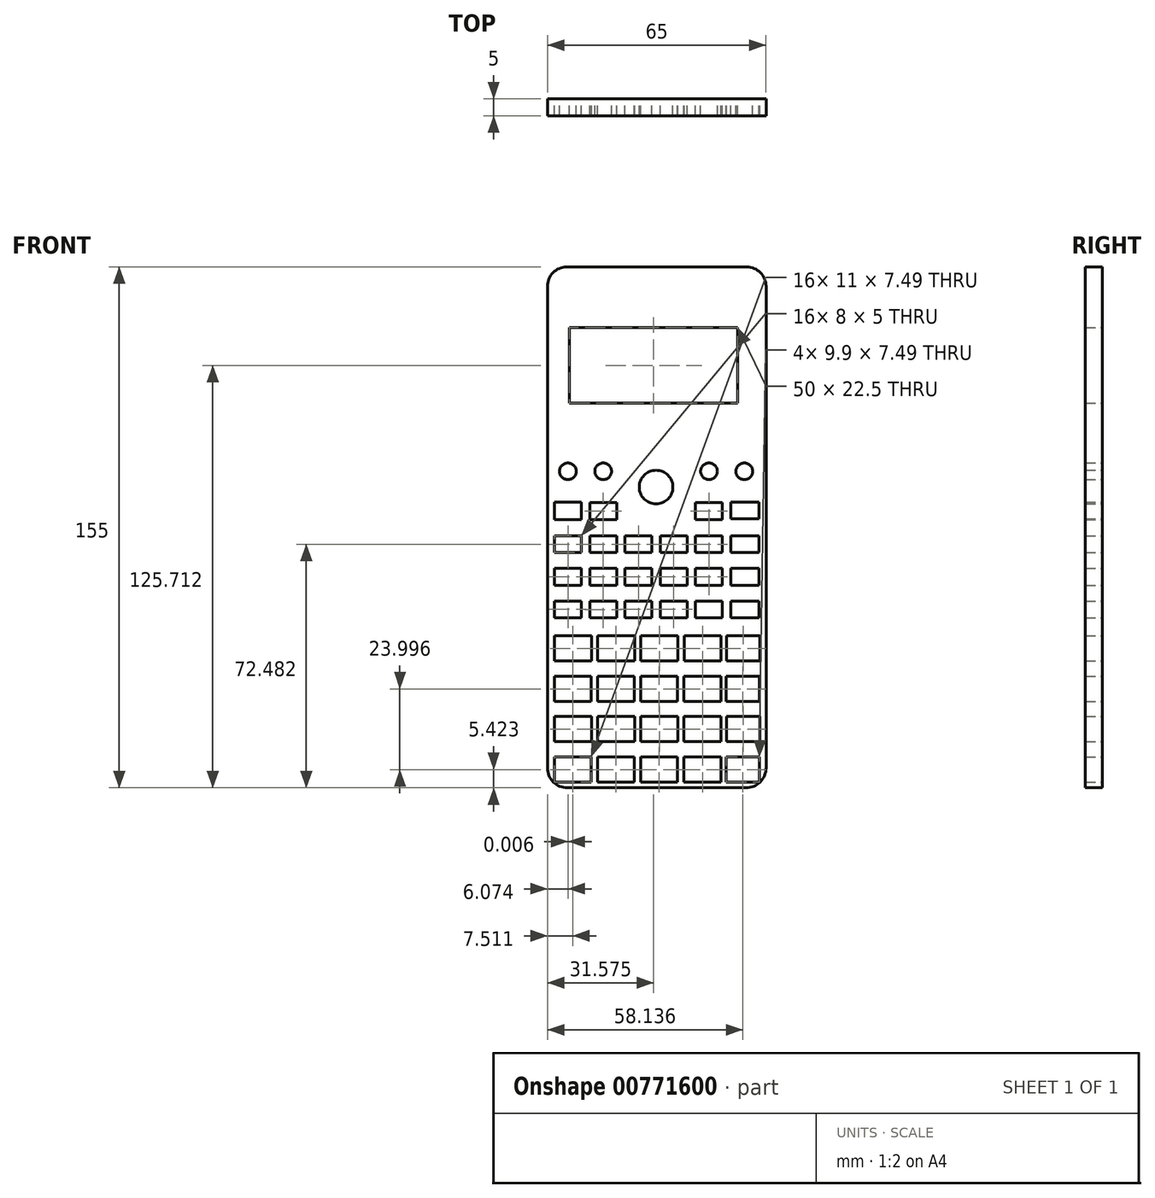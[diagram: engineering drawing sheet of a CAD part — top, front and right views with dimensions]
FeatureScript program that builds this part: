
annotation { "Feature Type Name" : "Feature", "Feature Type Description" : "" }
export const myFeature = defineFeature(function(context is Context, id is Id, definition is map)
    precondition{}
    {
        {
            var Q0;
            Q0=qCreatedBy(makeId("Front.planeOp"),FACE);
            var sketch = newSketch(context, id + "F0", { "sketchPlane" : qUnion([Q0])});
            skLineSegment(sketch, "E0.bottom", {"start": v(-32.07, 54.27) * mm, "end": v(32.93, 54.27) * mm});
            skLineSegment(sketch, "E0.top", {"start": v(-26.1, -45.56) * mm, "end": v(26.97, -45.56) * mm});
            skLineSegment(sketch, "E0.left", {"start": v(-32.07, 54.27) * mm, "end": v(-32.07, -39.6) * mm});
            skLineSegment(sketch, "E0.right", {"start": v(32.93, 54.27) * mm, "end": v(32.93, -39.6) * mm});
            skPoint(sketch, "E1.visualSharp", {"position": v(32.93, -45.56) * mm});
            skArc(sketch, "E1.filletArc", {"start": v(26.97, -45.56) * mm, "mid": v(31.19, -43.81) * mm, "end": v(32.93, -39.6) * mm});
            skPoint(sketch, "E2.visualSharp", {"position": v(-32.07, -45.56) * mm});
            skArc(sketch, "E2.filletArc", {"start": v(-32.07, -39.6) * mm, "mid": v(-30.32, -43.81) * mm, "end": v(-26.1, -45.56) * mm});
            skLineSegment(sketch, "E3", {"start": v(-30.06, -43.88) * mm, "end": v(-19.06, -43.88) * mm});
            skLineSegment(sketch, "E4", {"start": v(-19.06, -43.88) * mm, "end": v(-19.06, -36.4) * mm});
            skLineSegment(sketch, "E5", {"start": v(-19.06, -36.4) * mm, "end": v(-30.06, -36.4) * mm});
            skLineSegment(sketch, "E6", {"start": v(-30.06, -36.4) * mm, "end": v(-30.06, -43.88) * mm});
            skLineSegment(sketch, "E7", {"start": v(-30.06, -43.88) * mm, "end": v(-24.56, -43.88) * mm});
            skLineSegment(sketch, "E8", {"start": v(-17.22, -43.88) * mm, "end": v(-6.22, -43.88) * mm});
            skLineSegment(sketch, "E9", {"start": v(-6.22, -43.88) * mm, "end": v(-6.22, -36.4) * mm});
            skLineSegment(sketch, "E10", {"start": v(-6.22, -36.4) * mm, "end": v(-17.22, -36.4) * mm});
            skLineSegment(sketch, "E11", {"start": v(-17.22, -36.4) * mm, "end": v(-17.22, -43.88) * mm});
            skLineSegment(sketch, "E12", {"start": v(-17.22, -43.88) * mm, "end": v(-11.72, -43.88) * mm});
            skLineSegment(sketch, "E13", {"start": v(-4.36, -43.88) * mm, "end": v(6.63, -43.88) * mm});
            skLineSegment(sketch, "E14", {"start": v(6.63, -43.88) * mm, "end": v(6.63, -36.4) * mm});
            skLineSegment(sketch, "E15", {"start": v(6.63, -36.4) * mm, "end": v(-4.36, -36.4) * mm});
            skLineSegment(sketch, "E16", {"start": v(-4.36, -36.4) * mm, "end": v(-4.36, -43.88) * mm});
            skLineSegment(sketch, "E17", {"start": v(-4.36, -43.88) * mm, "end": v(1.14, -43.88) * mm});
            skLineSegment(sketch, "E18", {"start": v(8.52, -43.88) * mm, "end": v(19.52, -43.88) * mm});
            skLineSegment(sketch, "E19", {"start": v(19.52, -43.88) * mm, "end": v(19.52, -36.4) * mm});
            skLineSegment(sketch, "E20", {"start": v(19.52, -36.4) * mm, "end": v(8.52, -36.4) * mm});
            skLineSegment(sketch, "E21", {"start": v(8.52, -36.4) * mm, "end": v(8.52, -43.88) * mm});
            skLineSegment(sketch, "E22", {"start": v(8.52, -43.88) * mm, "end": v(14.02, -43.88) * mm});
            skLineSegment(sketch, "E23", {"start": v(21.12, -43.88) * mm, "end": v(31.02, -43.88) * mm});
            skLineSegment(sketch, "E24", {"start": v(31.02, -43.88) * mm, "end": v(31.02, -36.4) * mm});
            skLineSegment(sketch, "E25", {"start": v(31.02, -36.4) * mm, "end": v(21.12, -36.4) * mm});
            skLineSegment(sketch, "E26", {"start": v(21.12, -36.4) * mm, "end": v(21.12, -43.88) * mm});
            skLineSegment(sketch, "E27", {"start": v(21.12, -43.88) * mm, "end": v(25.78, -43.88) * mm});
            skLineSegment(sketch, "E28", {"start": v(-30, -31.8) * mm, "end": v(-19, -31.8) * mm});
            skLineSegment(sketch, "E29", {"start": v(-19, -31.8) * mm, "end": v(-19, -24.3) * mm});
            skLineSegment(sketch, "E30", {"start": v(-19, -24.3) * mm, "end": v(-30, -24.3) * mm});
            skLineSegment(sketch, "E31", {"start": v(-30, -24.3) * mm, "end": v(-30, -31.8) * mm});
            skLineSegment(sketch, "E32", {"start": v(-30, -31.8) * mm, "end": v(-24.5, -31.8) * mm});
            skLineSegment(sketch, "E33", {"start": v(-17.15, -31.8) * mm, "end": v(-6.16, -31.8) * mm});
            skLineSegment(sketch, "E34", {"start": v(-6.16, -31.8) * mm, "end": v(-6.16, -24.3) * mm});
            skLineSegment(sketch, "E35", {"start": v(-6.16, -24.3) * mm, "end": v(-17.15, -24.3) * mm});
            skLineSegment(sketch, "E36", {"start": v(-17.15, -24.3) * mm, "end": v(-17.15, -31.8) * mm});
            skLineSegment(sketch, "E37", {"start": v(-17.15, -31.8) * mm, "end": v(-11.66, -31.8) * mm});
            skLineSegment(sketch, "E38", {"start": v(-4.3, -31.8) * mm, "end": v(6.7, -31.8) * mm});
            skLineSegment(sketch, "E39", {"start": v(6.7, -31.8) * mm, "end": v(6.7, -24.3) * mm});
            skLineSegment(sketch, "E40", {"start": v(6.7, -24.3) * mm, "end": v(-4.3, -24.3) * mm});
            skLineSegment(sketch, "E41", {"start": v(-4.3, -24.3) * mm, "end": v(-4.3, -31.8) * mm});
            skLineSegment(sketch, "E42", {"start": v(-4.3, -31.8) * mm, "end": v(1.2, -31.8) * mm});
            skLineSegment(sketch, "E43", {"start": v(21.18, -31.8) * mm, "end": v(31.08, -31.8) * mm});
            skLineSegment(sketch, "E44", {"start": v(31.08, -31.8) * mm, "end": v(31.08, -24.3) * mm});
            skLineSegment(sketch, "E45", {"start": v(31.08, -24.3) * mm, "end": v(21.18, -24.3) * mm});
            skLineSegment(sketch, "E46", {"start": v(21.18, -24.3) * mm, "end": v(21.18, -31.8) * mm});
            skLineSegment(sketch, "E47", {"start": v(21.18, -31.8) * mm, "end": v(25.84, -31.8) * mm});
            skPoint(sketch, "E48.visualSharp", {"position": v(-32.07, -21.72) * mm});
            skLineSegment(sketch, "E49", {"start": v(-30.06, -19.89) * mm, "end": v(-19.06, -19.89) * mm});
            skLineSegment(sketch, "E50", {"start": v(-19.06, -19.89) * mm, "end": v(-19.06, -12.4) * mm});
            skLineSegment(sketch, "E51", {"start": v(-19.06, -12.4) * mm, "end": v(-30.06, -12.4) * mm});
            skLineSegment(sketch, "E52", {"start": v(-30.06, -12.4) * mm, "end": v(-30.06, -19.89) * mm});
            skLineSegment(sketch, "E53", {"start": v(-30.06, -19.89) * mm, "end": v(-24.56, -19.89) * mm});
            skLineSegment(sketch, "E54", {"start": v(-17.22, -19.89) * mm, "end": v(-6.22, -19.89) * mm});
            skLineSegment(sketch, "E55", {"start": v(-6.22, -19.89) * mm, "end": v(-6.22, -12.4) * mm});
            skLineSegment(sketch, "E56", {"start": v(-6.22, -12.4) * mm, "end": v(-17.22, -12.4) * mm});
            skLineSegment(sketch, "E57", {"start": v(-17.22, -12.4) * mm, "end": v(-17.22, -19.89) * mm});
            skLineSegment(sketch, "E58", {"start": v(-17.22, -19.89) * mm, "end": v(-11.72, -19.89) * mm});
            skLineSegment(sketch, "E59", {"start": v(-4.36, -19.89) * mm, "end": v(6.63, -19.89) * mm});
            skLineSegment(sketch, "E60", {"start": v(6.63, -19.89) * mm, "end": v(6.63, -12.4) * mm});
            skLineSegment(sketch, "E61", {"start": v(6.63, -12.4) * mm, "end": v(-4.36, -12.4) * mm});
            skLineSegment(sketch, "E62", {"start": v(-4.36, -12.4) * mm, "end": v(-4.36, -19.89) * mm});
            skLineSegment(sketch, "E63", {"start": v(-4.36, -19.89) * mm, "end": v(1.14, -19.89) * mm});
            skLineSegment(sketch, "E64", {"start": v(8.52, -19.89) * mm, "end": v(19.52, -19.89) * mm});
            skLineSegment(sketch, "E65", {"start": v(19.52, -19.89) * mm, "end": v(19.52, -12.4) * mm});
            skLineSegment(sketch, "E66", {"start": v(19.52, -12.4) * mm, "end": v(8.52, -12.4) * mm});
            skLineSegment(sketch, "E67", {"start": v(8.52, -12.4) * mm, "end": v(8.52, -19.89) * mm});
            skLineSegment(sketch, "E68", {"start": v(8.52, -19.89) * mm, "end": v(14.02, -19.89) * mm});
            skLineSegment(sketch, "E69", {"start": v(21.12, -19.89) * mm, "end": v(31.02, -19.89) * mm});
            skLineSegment(sketch, "E70", {"start": v(31.02, -19.89) * mm, "end": v(31.02, -12.4) * mm});
            skLineSegment(sketch, "E71", {"start": v(31.02, -12.4) * mm, "end": v(21.12, -12.4) * mm});
            skLineSegment(sketch, "E72", {"start": v(21.12, -12.4) * mm, "end": v(21.12, -19.89) * mm});
            skLineSegment(sketch, "E73", {"start": v(21.12, -19.89) * mm, "end": v(25.78, -19.89) * mm});
            skLineSegment(sketch, "E74", {"start": v(-30, -7.8) * mm, "end": v(-19, -7.8) * mm});
            skLineSegment(sketch, "E75", {"start": v(-19, -7.8) * mm, "end": v(-19, -0.31) * mm});
            skLineSegment(sketch, "E76", {"start": v(-19, -0.31) * mm, "end": v(-30, -0.31) * mm});
            skLineSegment(sketch, "E77", {"start": v(-30, -0.31) * mm, "end": v(-30, -7.8) * mm});
            skLineSegment(sketch, "E78", {"start": v(-30, -7.8) * mm, "end": v(-24.5, -7.8) * mm});
            skLineSegment(sketch, "E79", {"start": v(-17.15, -7.8) * mm, "end": v(-6.16, -7.8) * mm});
            skLineSegment(sketch, "E80", {"start": v(-6.16, -7.8) * mm, "end": v(-6.16, -0.31) * mm});
            skLineSegment(sketch, "E81", {"start": v(-6.16, -0.31) * mm, "end": v(-17.15, -0.31) * mm});
            skLineSegment(sketch, "E82", {"start": v(-17.15, -0.31) * mm, "end": v(-17.15, -7.8) * mm});
            skLineSegment(sketch, "E83", {"start": v(-17.15, -7.8) * mm, "end": v(-11.66, -7.8) * mm});
            skLineSegment(sketch, "E84", {"start": v(-4.3, -7.8) * mm, "end": v(6.7, -7.8) * mm});
            skLineSegment(sketch, "E85", {"start": v(6.7, -7.8) * mm, "end": v(6.7, -0.31) * mm});
            skLineSegment(sketch, "E86", {"start": v(6.7, -0.31) * mm, "end": v(-4.3, -0.31) * mm});
            skLineSegment(sketch, "E87", {"start": v(-4.3, -0.31) * mm, "end": v(-4.3, -7.8) * mm});
            skLineSegment(sketch, "E88", {"start": v(-4.3, -7.8) * mm, "end": v(1.2, -7.8) * mm});
            skLineSegment(sketch, "E89", {"start": v(8.58, -7.8) * mm, "end": v(19.58, -7.8) * mm});
            skLineSegment(sketch, "E90", {"start": v(19.58, -7.8) * mm, "end": v(19.58, -0.31) * mm});
            skLineSegment(sketch, "E91", {"start": v(19.58, -0.31) * mm, "end": v(8.58, -0.31) * mm});
            skLineSegment(sketch, "E92", {"start": v(8.58, -0.31) * mm, "end": v(8.58, -7.8) * mm});
            skLineSegment(sketch, "E93", {"start": v(8.58, -7.8) * mm, "end": v(14.08, -7.8) * mm});
            skLineSegment(sketch, "E94", {"start": v(21.18, -7.8) * mm, "end": v(31.08, -7.8) * mm});
            skLineSegment(sketch, "E95", {"start": v(31.08, -7.8) * mm, "end": v(31.08, -0.31) * mm});
            skLineSegment(sketch, "E96", {"start": v(31.08, -0.31) * mm, "end": v(21.18, -0.31) * mm});
            skLineSegment(sketch, "E97", {"start": v(21.18, -0.31) * mm, "end": v(21.18, -7.8) * mm});
            skLineSegment(sketch, "E98", {"start": v(21.18, -7.8) * mm, "end": v(25.84, -7.8) * mm});
            skLineSegment(sketch, "E99", {"start": v(-30, 5.02) * mm, "end": v(-21.99, 5.02) * mm});
            skLineSegment(sketch, "E100", {"start": v(-21.99, 5.02) * mm, "end": v(-21.99, 10.02) * mm});
            skLineSegment(sketch, "E101", {"start": v(-21.99, 10.02) * mm, "end": v(-30, 10.02) * mm});
            skLineSegment(sketch, "E102", {"start": v(-30, 10.02) * mm, "end": v(-30, 5.02) * mm});
            skLineSegment(sketch, "E103", {"start": v(-30, 5.02) * mm, "end": v(-27.64, 5.02) * mm});
            skLineSegment(sketch, "E104", {"start": v(-19.5, 5.02) * mm, "end": v(-11.5, 5.02) * mm});
            skLineSegment(sketch, "E105", {"start": v(-11.5, 5.02) * mm, "end": v(-11.5, 10.02) * mm});
            skLineSegment(sketch, "E106", {"start": v(-11.5, 10.02) * mm, "end": v(-19.5, 10.02) * mm});
            skLineSegment(sketch, "E107", {"start": v(-19.5, 10.02) * mm, "end": v(-19.5, 5.02) * mm});
            skLineSegment(sketch, "E108", {"start": v(-19.5, 5.02) * mm, "end": v(-17.15, 5.02) * mm});
            skLineSegment(sketch, "E109", {"start": v(-9.01, 5.02) * mm, "end": v(-1, 5.02) * mm});
            skLineSegment(sketch, "E110", {"start": v(-1, 5.02) * mm, "end": v(-1, 10.02) * mm});
            skLineSegment(sketch, "E111", {"start": v(-1, 10.02) * mm, "end": v(-9.01, 10.02) * mm});
            skLineSegment(sketch, "E112", {"start": v(-9.01, 10.02) * mm, "end": v(-9.01, 5.02) * mm});
            skLineSegment(sketch, "E113", {"start": v(-9.01, 5.02) * mm, "end": v(-7.18, 5.02) * mm});
            skLineSegment(sketch, "E114", {"start": v(1.48, 5.02) * mm, "end": v(9.48, 5.02) * mm});
            skLineSegment(sketch, "E115", {"start": v(9.48, 5.02) * mm, "end": v(9.48, 10.02) * mm});
            skLineSegment(sketch, "E116", {"start": v(9.48, 10.02) * mm, "end": v(1.48, 10.02) * mm});
            skLineSegment(sketch, "E117", {"start": v(1.48, 10.02) * mm, "end": v(1.48, 5.02) * mm});
            skLineSegment(sketch, "E118", {"start": v(11.97, 5.02) * mm, "end": v(19.97, 5.02) * mm});
            skLineSegment(sketch, "E119", {"start": v(19.97, 5.02) * mm, "end": v(19.97, 10) * mm});
            skLineSegment(sketch, "E120", {"start": v(19.97, 10) * mm, "end": v(11.97, 10) * mm});
            skLineSegment(sketch, "E121", {"start": v(11.97, 10) * mm, "end": v(11.97, 5.02) * mm});
            skLineSegment(sketch, "E122", {"start": v(11.97, 5.02) * mm, "end": v(12.82, 5.02) * mm});
            skLineSegment(sketch, "E123", {"start": v(22.46, 5) * mm, "end": v(30.8, 5) * mm});
            skLineSegment(sketch, "E124", {"start": v(30.8, 5) * mm, "end": v(30.8, 10) * mm});
            skLineSegment(sketch, "E125", {"start": v(30.8, 10) * mm, "end": v(22.46, 10) * mm});
            skLineSegment(sketch, "E126", {"start": v(22.46, 10) * mm, "end": v(22.46, 5) * mm});
            skLineSegment(sketch, "E127", {"start": v(22.46, 5) * mm, "end": v(24.85, 5) * mm});
            skLineSegment(sketch, "E128", {"start": v(-29.99, 14.72) * mm, "end": v(-21.99, 14.72) * mm});
            skLineSegment(sketch, "E129", {"start": v(-21.99, 14.72) * mm, "end": v(-21.99, 19.73) * mm});
            skLineSegment(sketch, "E130", {"start": v(-21.99, 19.73) * mm, "end": v(-29.99, 19.73) * mm});
            skLineSegment(sketch, "E131", {"start": v(-29.99, 19.73) * mm, "end": v(-29.99, 14.72) * mm});
            skLineSegment(sketch, "E132", {"start": v(-29.99, 14.72) * mm, "end": v(-26.28, 14.72) * mm});
            skLineSegment(sketch, "E133", {"start": v(-19.5, 14.72) * mm, "end": v(-11.5, 14.72) * mm});
            skLineSegment(sketch, "E134", {"start": v(-11.5, 14.72) * mm, "end": v(-11.5, 19.73) * mm});
            skLineSegment(sketch, "E135", {"start": v(-11.5, 19.73) * mm, "end": v(-19.5, 19.73) * mm});
            skLineSegment(sketch, "E136", {"start": v(-19.5, 19.73) * mm, "end": v(-19.5, 14.72) * mm});
            skLineSegment(sketch, "E137", {"start": v(-19.5, 14.72) * mm, "end": v(-15.48, 14.72) * mm});
            skLineSegment(sketch, "E138", {"start": v(-9, 14.72) * mm, "end": v(-1, 14.72) * mm});
            skLineSegment(sketch, "E139", {"start": v(-1, 14.72) * mm, "end": v(-1, 19.73) * mm});
            skLineSegment(sketch, "E140", {"start": v(-1, 19.73) * mm, "end": v(-9, 19.73) * mm});
            skLineSegment(sketch, "E141", {"start": v(-9, 19.73) * mm, "end": v(-9, 14.72) * mm});
            skLineSegment(sketch, "E142", {"start": v(-9, 14.72) * mm, "end": v(-5.82, 14.72) * mm});
            skLineSegment(sketch, "E143", {"start": v(1.48, 14.72) * mm, "end": v(9.48, 14.72) * mm});
            skLineSegment(sketch, "E144", {"start": v(9.48, 14.72) * mm, "end": v(9.48, 19.73) * mm});
            skLineSegment(sketch, "E145", {"start": v(9.48, 19.73) * mm, "end": v(1.48, 19.73) * mm});
            skLineSegment(sketch, "E146", {"start": v(1.48, 19.73) * mm, "end": v(1.48, 14.72) * mm});
            skLineSegment(sketch, "E147", {"start": v(11.97, 14.72) * mm, "end": v(19.97, 14.72) * mm});
            skLineSegment(sketch, "E148", {"start": v(19.97, 14.72) * mm, "end": v(19.97, 19.73) * mm});
            skLineSegment(sketch, "E149", {"start": v(19.97, 19.73) * mm, "end": v(11.97, 19.73) * mm});
            skLineSegment(sketch, "E150", {"start": v(11.97, 19.73) * mm, "end": v(11.97, 14.72) * mm});
            skLineSegment(sketch, "E151", {"start": v(11.97, 14.72) * mm, "end": v(14.18, 14.72) * mm});
            skLineSegment(sketch, "E152", {"start": v(22.46, 14.72) * mm, "end": v(30.8, 14.72) * mm});
            skLineSegment(sketch, "E153", {"start": v(30.8, 14.72) * mm, "end": v(30.8, 19.73) * mm});
            skLineSegment(sketch, "E154", {"start": v(30.8, 19.73) * mm, "end": v(22.46, 19.73) * mm});
            skLineSegment(sketch, "E155", {"start": v(22.46, 19.73) * mm, "end": v(22.46, 14.72) * mm});
            skLineSegment(sketch, "E156", {"start": v(22.46, 14.72) * mm, "end": v(26.17, 14.72) * mm});
            skLineSegment(sketch, "E157", {"start": v(-30, 24.42) * mm, "end": v(-22, 24.42) * mm});
            skLineSegment(sketch, "E158", {"start": v(-22, 24.42) * mm, "end": v(-22, 29.42) * mm});
            skLineSegment(sketch, "E159", {"start": v(-22, 29.42) * mm, "end": v(-30, 29.42) * mm});
            skLineSegment(sketch, "E160", {"start": v(-30, 29.42) * mm, "end": v(-30, 24.42) * mm});
            skLineSegment(sketch, "E161", {"start": v(-30, 24.42) * mm, "end": v(-25.98, 24.42) * mm});
            skLineSegment(sketch, "E162", {"start": v(-19.5, 24.42) * mm, "end": v(-11.5, 24.42) * mm});
            skLineSegment(sketch, "E163", {"start": v(-11.5, 24.42) * mm, "end": v(-11.5, 29.42) * mm});
            skLineSegment(sketch, "E164", {"start": v(-11.5, 29.42) * mm, "end": v(-19.5, 29.42) * mm});
            skLineSegment(sketch, "E165", {"start": v(-19.5, 29.42) * mm, "end": v(-19.5, 24.42) * mm});
            skLineSegment(sketch, "E166", {"start": v(-19.5, 24.42) * mm, "end": v(-15.5, 24.42) * mm});
            skLineSegment(sketch, "E167", {"start": v(-9.02, 24.42) * mm, "end": v(-1.02, 24.42) * mm});
            skLineSegment(sketch, "E168", {"start": v(-1.02, 24.42) * mm, "end": v(-1.02, 29.42) * mm});
            skLineSegment(sketch, "E169", {"start": v(-1.02, 29.42) * mm, "end": v(-9.02, 29.42) * mm});
            skLineSegment(sketch, "E170", {"start": v(-9.02, 29.42) * mm, "end": v(-9.02, 24.42) * mm});
            skLineSegment(sketch, "E171", {"start": v(-9.02, 24.42) * mm, "end": v(-5.52, 24.42) * mm});
            skLineSegment(sketch, "E172", {"start": v(1.47, 24.42) * mm, "end": v(9.47, 24.42) * mm});
            skLineSegment(sketch, "E173", {"start": v(9.47, 24.42) * mm, "end": v(9.47, 29.42) * mm});
            skLineSegment(sketch, "E174", {"start": v(9.47, 29.42) * mm, "end": v(1.47, 29.42) * mm});
            skLineSegment(sketch, "E175", {"start": v(1.47, 29.42) * mm, "end": v(1.47, 24.42) * mm});
            skLineSegment(sketch, "E176", {"start": v(11.96, 24.42) * mm, "end": v(19.97, 24.42) * mm});
            skLineSegment(sketch, "E177", {"start": v(19.97, 24.42) * mm, "end": v(19.97, 29.42) * mm});
            skLineSegment(sketch, "E178", {"start": v(19.97, 29.42) * mm, "end": v(11.96, 29.42) * mm});
            skLineSegment(sketch, "E179", {"start": v(11.96, 29.42) * mm, "end": v(11.96, 24.42) * mm});
            skLineSegment(sketch, "E180", {"start": v(11.96, 24.42) * mm, "end": v(14.48, 24.42) * mm});
            skLineSegment(sketch, "E181", {"start": v(22.45, 24.42) * mm, "end": v(30.8, 24.42) * mm});
            skLineSegment(sketch, "E182", {"start": v(30.8, 24.42) * mm, "end": v(30.8, 29.42) * mm});
            skLineSegment(sketch, "E183", {"start": v(30.8, 29.42) * mm, "end": v(22.45, 29.42) * mm});
            skLineSegment(sketch, "E184", {"start": v(22.45, 29.42) * mm, "end": v(22.45, 24.42) * mm});
            skLineSegment(sketch, "E185", {"start": v(22.45, 24.42) * mm, "end": v(26.47, 24.42) * mm});
            skLineSegment(sketch, "E186", {"start": v(-30, 34.28) * mm, "end": v(-22, 34.28) * mm});
            skLineSegment(sketch, "E187", {"start": v(-22, 34.28) * mm, "end": v(-22, 39.45) * mm});
            skLineSegment(sketch, "E188", {"start": v(-22, 39.45) * mm, "end": v(-30, 39.45) * mm});
            skLineSegment(sketch, "E189", {"start": v(-30, 39.45) * mm, "end": v(-30, 34.28) * mm});
            skLineSegment(sketch, "E190", {"start": v(-30, 34.28) * mm, "end": v(-25.98, 34.28) * mm});
            skLineSegment(sketch, "E191", {"start": v(-19.5, 34.28) * mm, "end": v(-11.5, 34.28) * mm});
            skLineSegment(sketch, "E192", {"start": v(-11.5, 34.28) * mm, "end": v(-11.5, 39.28) * mm});
            skLineSegment(sketch, "E193", {"start": v(-11.5, 39.28) * mm, "end": v(-19.5, 39.28) * mm});
            skLineSegment(sketch, "E194", {"start": v(-19.5, 39.28) * mm, "end": v(-19.5, 34.28) * mm});
            skLineSegment(sketch, "E195", {"start": v(-19.5, 34.28) * mm, "end": v(-15.5, 34.28) * mm});
            skLineSegment(sketch, "E196", {"start": v(11.96, 34.28) * mm, "end": v(19.97, 34.28) * mm});
            skLineSegment(sketch, "E197", {"start": v(19.97, 34.28) * mm, "end": v(19.97, 39.28) * mm});
            skLineSegment(sketch, "E198", {"start": v(19.97, 39.28) * mm, "end": v(11.96, 39.28) * mm});
            skLineSegment(sketch, "E199", {"start": v(11.96, 39.28) * mm, "end": v(11.96, 34.28) * mm});
            skLineSegment(sketch, "E200", {"start": v(11.96, 34.28) * mm, "end": v(14.48, 34.28) * mm});
            skLineSegment(sketch, "E201", {"start": v(22.45, 34.45) * mm, "end": v(30.8, 34.45) * mm});
            skLineSegment(sketch, "E202", {"start": v(30.8, 34.45) * mm, "end": v(30.8, 39.45) * mm});
            skLineSegment(sketch, "E203", {"start": v(30.8, 39.45) * mm, "end": v(22.45, 39.45) * mm});
            skLineSegment(sketch, "E204", {"start": v(22.45, 39.45) * mm, "end": v(22.45, 34.45) * mm});
            skLineSegment(sketch, "E205", {"start": v(22.45, 34.45) * mm, "end": v(26.47, 34.45) * mm});
            skLineSegment(sketch, "E206", {"start": v(9.47, 24.42) * mm, "end": v(9.47, 26.93) * mm});
            skCircle(sketch, "E207", {"center": v(-15.5, 48.63) * mm, "radius": 2.49 * mm});
            skCircle(sketch, "E208", {"center": v(0.23, 43.93) * mm, "radius": 5 * mm});
            skLineSegment(sketch, "E209", {"start": v(11.96, 34.28) * mm, "end": v(15.96, 34.28) * mm});
            skCircle(sketch, "E210", {"center": v(15.96, 48.63) * mm, "radius": 2.49 * mm});
            skCircle(sketch, "E211", {"center": v(26.47, 48.63) * mm, "radius": 2.49 * mm});
            skCircle(sketch, "E212", {"center": v(-26, 48.63) * mm, "radius": 2.49 * mm});
            skLineSegment(sketch, "E213", {"start": v(-4.3, -24.3) * mm, "end": v(6.7, -24.3) * mm});
            skLineSegment(sketch, "E214", {"start": v(8.52, -24.3) * mm, "end": v(8.52, -31.8) * mm});
            skLineSegment(sketch, "E215", {"start": v(8.52, -31.8) * mm, "end": v(19.52, -31.8) * mm});
            skLineSegment(sketch, "E216", {"start": v(19.52, -31.8) * mm, "end": v(19.52, -24.3) * mm});
            skLineSegment(sketch, "E217", {"start": v(19.52, -24.3) * mm, "end": v(8.52, -24.3) * mm});
            skLineSegment(sketch, "E218", {"start": v(-32.07, 54.27) * mm, "end": v(-32.07, 103.68) * mm});
            skArc(sketch, "E219", {"start": v(-26.3, 109.44) * mm, "mid": v(-30.38, 107.76) * mm, "end": v(-32.07, 103.68) * mm});
            skLineSegment(sketch, "E220", {"start": v(32.93, 103.68) * mm, "end": v(32.93, 54.27) * mm});
            skArc(sketch, "E221", {"start": v(32.93, 103.68) * mm, "mid": v(31.24, 107.76) * mm, "end": v(27.17, 109.44) * mm});
            skLineSegment(sketch, "E222", {"start": v(-26.3, 109.44) * mm, "end": v(27.17, 109.44) * mm});
            skLineSegment(sketch, "E223.bottom", {"start": v(-25.5, 91.4) * mm, "end": v(24.5, 91.4) * mm});
            skLineSegment(sketch, "E223.top", {"start": v(-25.5, 68.9) * mm, "end": v(24.5, 68.9) * mm});
            skLineSegment(sketch, "E223.left", {"start": v(-25.5, 91.4) * mm, "end": v(-25.5, 68.9) * mm});
            skLineSegment(sketch, "E223.right", {"start": v(24.5, 91.4) * mm, "end": v(24.5, 68.9) * mm});
            skSolve(sketch);
        }
        {
            var Q0;
            Q0=makeQuery(id+"F0.imprint","IMPRINT",FACE,{"disambiguationData":[TD([[makeQuery(id+"F0.imprint","IMPRINT",EDGE,{"derivedFrom":sQuery(id+"F0.wireOp",EDGE,"E0.bottom")}),-1.0]])]});
            extrude(context, id + "F1", {"entities" : qUnion([Q0]), "depth" : 5 * mm, "offsetDistance" : 25 * mm});
        }
        {
            var Q0;
            Q0=makeQuery(id+"F0.imprint","IMPRINT",FACE,{"disambiguationData":[TD([[makeQuery(id+"F0.imprint","IMPRINT",EDGE,{"derivedFrom":sQuery(id+"F0.wireOp",EDGE,"E0.bottom")}),1.0]])]});
            extrude(context, id + "F2", {"entities" : qUnion([Q0]), "operationType" : NewBodyOperationType.ADD, "depth" : 5 * mm, "offsetDistance" : 25 * mm});
        }
    });
